# Revit family: Comfort Ribbed 600mm WH Oak Cabinet 1 Drawer
name_source: partatom
category: Plumbing Fixtures
units: mm (PartAtom-declared; Revit-internal decimal feet)

## family parameters
Always vertical = Yes
Cut with Voids When Loaded = No
Enable Cutting in Views = No
Maintain Annotation Orientation = No
OmniClass Number = 23.45.00.00
OmniClass Title = Sanitary, Laundry, and Cleaning Equipment
Part Type = Normal
Room Calculation Point = No
Round Connector Dimension = Use Diameter
Shared = No
Work Plane-Based = No

## types (2) — shared parameters
Carcass = Oak
Category = Cabinets
Colour = Oak
Door Base = Oak
Manufacturer = Lecico SA
Notes = Dimensions are of Cabinet Only
Slats = Oak
Stone = Sintered Stone
Technical Dimensions = W560 x H400 x D460mm
URL = https://www.lecicosa.co.za
zero-valued in all types: Default Elevation

## per-type parameters (varying)
| type | Material | Product Code | Sintered Stone | Vanity |
| Comfort Ribbed 600mm WH Oak Cabinet 1 Drawer + 600 White Curved Slab Top | MDF with Melamine Finish + Sintered Stone | CABCOMFWH0600BC + SLA600CURWHITBC | Yes | No |
| Comfort Ribbed 600mm WH Oak Cabinet 1 Drawer + Matrix Vanity Basin | MDF with Melamine Finish + Vitreous China | CABCOMFWH0600BC + MATBASVAN1600UE | No | Yes |

note: column(s) folded — value = type name in every type: Model

## geometry (parser evidence)
native form markers: Sweep x5
no freeform markers — native parametric forms only
